# Revit family: HVAC_Air-Conditioning_Friedrich_Variable-Refrigerant-Packaged-Heat-Pump_VRP07-1
name_source: partatom
category: Mechanical Equipment
revit_build: Autodesk Revit 2018 (Build: 20170223_1515(x64)
units: mm (PartAtom-declared; Revit-internal decimal feet)

## family parameters
Always vertical = Yes
Cut with Voids When Loaded = No
OmniClass Number = 23.75.10.24.21.27.21
OmniClass Title = Packaged Terminal Air Conditioning Units
Part Type = Normal
Room Calculation Point = No
Round Connector Dimension = Use Diameter
Shared = No
Work Plane-Based = No

## types (3) — shared parameters
Air Flow = 360.0 CFM
Air Supply Depth = 5 "
Air Supply Width = 21 "
BIMobject category = Air Conditioning
BIMobject category code = hvac-air-con
BIMobject main category = HVAC
BIMobject main category code = hvac
COP = 3.3
Clearance box height = 46.47 "
Clearance box material = Clearance Box - Red
Cooling = 7000 Btu/h
Cooling Current = 3 A
Cooling Range = 3800-10000
Depth = 22.81 "
Description = Precision Inverter® compressor delivers best in class cooling performance with efficiencies up to 20 SEER. Super efficient heating with low-ambient heat pump operation to 0˚ F*.
Design country = United States
EER Rating = 11
Edition number = 1
Filter Material = Filter - Friedrich - Grey
Heat Pump Current = 3 A
Heating Power = 621 W
Heating Seasonal Performance Factor = 8.6
Height = 44.94 "
IFC Classification = Air Terminal
Installation instructions = https://f.hubspotusercontent40.net
Load Classification = HVAC
Main Material = Metal - Friedrich - White
Manufacturer = Friedrich
Manufacturer country = Mexico
Manufacturer name = Friedrich
Masterformat 2014 Code = 23 81 13
Masterformat 2014 Description = Packaged Terminal Air-Conditioners
Material main = Metal
NBS Reference Code = 68-38
NBS Reference Description = Heat Pumps
Nominal height = 45 "
Nominal width = 23 "
OmniClass Code = 23-33 17 00
OmniClass Description = Heat Pumps
Outdoor Operating Range = 55-115
Product Guid = 12b9b913-be3b-4e87-a701-d458c0ca17a4
Product SKU = VRP07
Product certification = https://f.hubspotusercontent40.net
Product data url = https://www.bimobject.com
Product family = Variable Refrigerant Package
Product group = VRP
Product name = VRP Variable Refrigerant Packaged Heat Pump (7,000 BTU/h)
Product url = https://www.friedrich.com
QR code = https://www.bimobject.com
Return Air Depth = 14 "
Return Air Width = 20 "
SEER = 15.5
Technical description = https://f.hubspotusercontent40.net
Total Heating Capacity = 7000 Btu/h
UNSPSC Code = 40101806
URL = https://www.friedrich.com
Uniclass 1.4 Code = L7524
Uniclass 1.4 Description = Heat pumps
Uniclass 2.0 Code = PR-68-38
Uniclass 2.0 Description = Heat Pumps
Uniclass 2015 Code = Pr_70_60_37
Uniclass 2015 Name = Heat pumps
Uniformat II Code = D3050
Uniformat II Description = Terminal & Package Units
Weight = 161.00 lbm
Weight Net (Kg) = 73
Width = 22.94 "
Youtube clip = https://youtu.be

## per-type parameters (varying)
| type | Model | Voltage | Voltage Range |
| VRP07 K 230V | VRP07K | 230 V | 208 - 230 V |
| VRP07 K 208V | VRP07K | 208 V | 208 - 230 V |
| VRP07 R 265V | VRP07R | 265 V | 265 V |

## geometry (parser evidence)
native form markers: Sweep x4
no freeform markers — native parametric forms only
